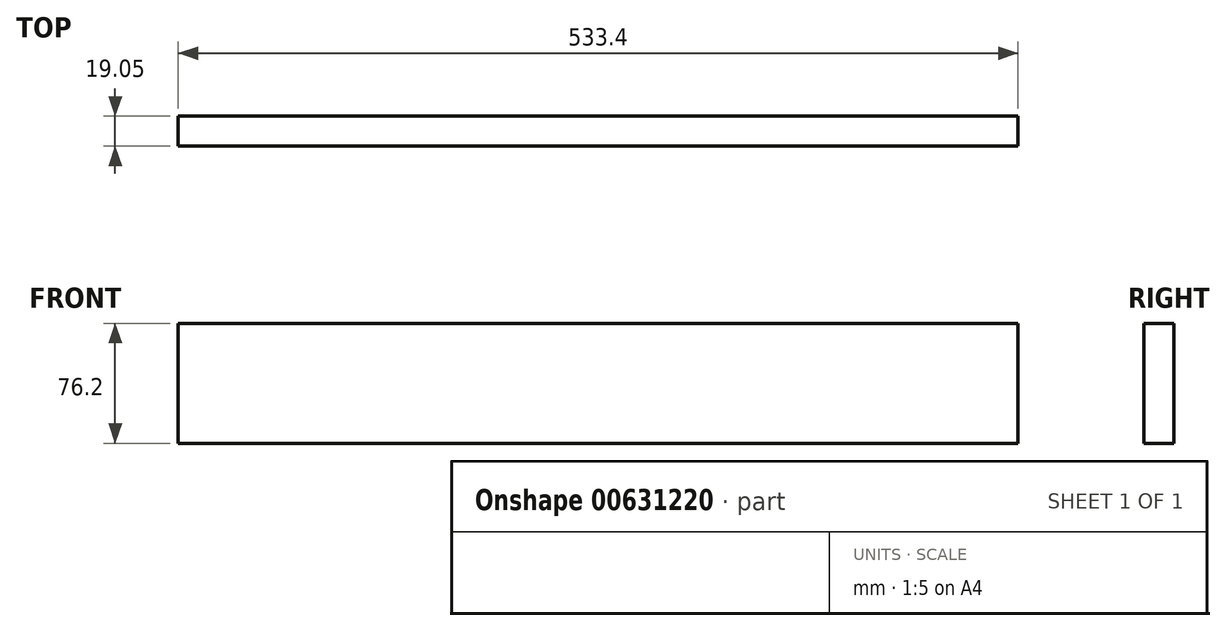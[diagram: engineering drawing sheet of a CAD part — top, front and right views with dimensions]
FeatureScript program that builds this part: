
annotation { "Feature Type Name" : "Feature", "Feature Type Description" : "" }
export const myFeature = defineFeature(function(context is Context, id is Id, definition is map)
    precondition{}
    {
        {
            var Q0;
            Q0=qCreatedBy(makeId("Front.planeOp"),FACE);
            var sketch = newSketch(context, id + "F0", { "sketchPlane" : qUnion([Q0])});
            skLineSegment(sketch, "E0.bottom", {"start": v(0, 0) * mm, "end": v(533.4, 0) * mm});
            skLineSegment(sketch, "E0.top", {"start": v(0, 76.2) * mm, "end": v(533.4, 76.2) * mm});
            skLineSegment(sketch, "E0.left", {"start": v(0, 0) * mm, "end": v(0, 76.2) * mm});
            skLineSegment(sketch, "E0.right", {"start": v(533.4, 0) * mm, "end": v(533.4, 76.2) * mm});
            skSolve(sketch);
        }
        {
            var Q0;
            Q0=qSketchRegion(id+"Fzz42SO8jX8z24B_0",true);
            var Q1;
            Q1=makeQuery(id+"F0.imprint","IMPRINT",FACE,{"disambiguationData":[TD([[makeQuery(id+"F0.imprint","IMPRINT",EDGE,{"derivedFrom":sQuery(id+"F0.wireOp",EDGE,"E0.bottom")}),1.0]])]});
            extrude(context, id + "F1", {"entities" : qUnion([Q0, Q1]), "depth" : -19.05 * mm, "offsetDistance" : 25.4 * mm});
        }
    });
